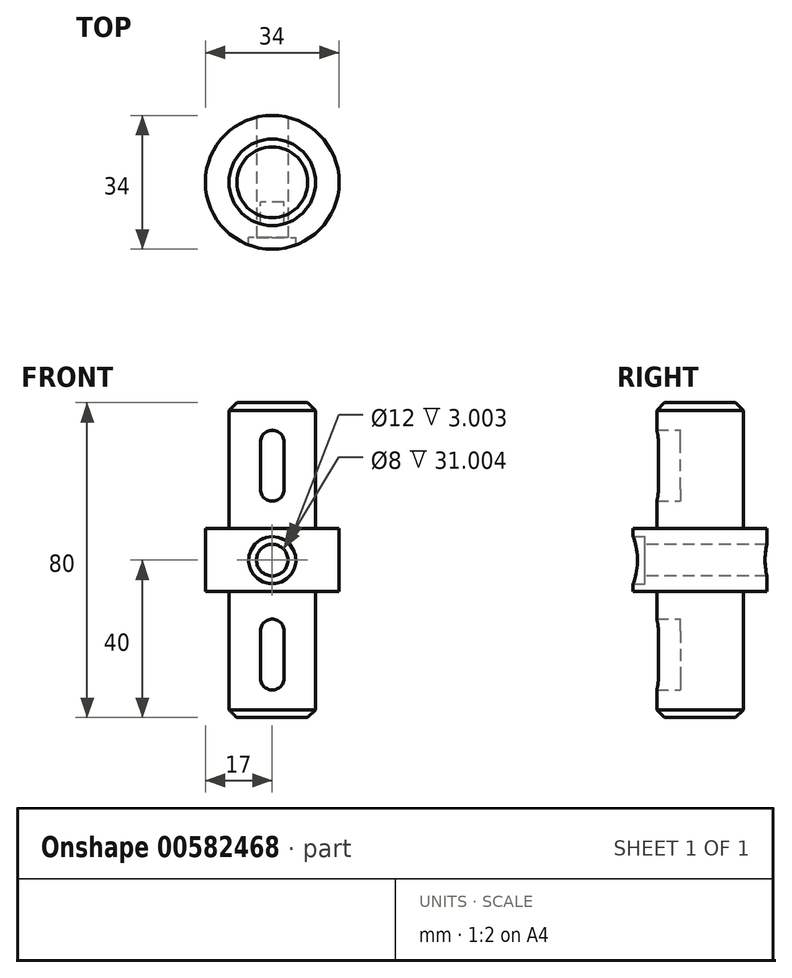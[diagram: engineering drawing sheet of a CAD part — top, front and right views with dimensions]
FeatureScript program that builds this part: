
annotation { "Feature Type Name" : "Feature", "Feature Type Description" : "" }
export const myFeature = defineFeature(function(context is Context, id is Id, definition is map)
    precondition{}
    {
        {
            var Q0;
            Q0=qCreatedBy(makeId("Top.planeOp"),FACE);
            var sketch = newSketch(context, id + "F0", { "sketchPlane" : qUnion([Q0])});
            skCircle(sketch, "E0", {"center": v(0, 0) * mm, "radius": 17 * mm});
            skSolve(sketch);
        }
        {
            var Q0;
            Q0=makeQuery(id+"F0.imprint","IMPRINT",FACE,{"disambiguationData":[TD([[makeQuery(id+"F0.imprint","IMPRINT",EDGE,{"derivedFrom":sQuery(id+"F0.wireOp",EDGE,"E0")}),1.0]])]});
            extrude(context, id + "F1", {"entities" : qUnion([Q0]), "depth" : 16 * mm, "offsetDistance" : 25 * mm});
        }
        {
            var Q0;
            Q0=makeQuery(id+"F1.opExtrude","CAP_FACE",FACE,{"disambiguationData":[OSD([sQuery(id+"F0.wireOp",EDGE,"E0")])],"isStart":false});
            var sketch = newSketch(context, id + "F2", { "sketchPlane" : qUnion([Q0])});
            skCircle(sketch, "E1", {"center": v(0, 0) * mm, "radius": 11 * mm});
            skSolve(sketch);
        }
        {
            var Q0;
            Q0=makeQuery(id+"F2.imprint","IMPRINT",FACE,{"disambiguationData":[TD([[makeQuery(id+"F2.imprint","IMPRINT",EDGE,{"derivedFrom":sQuery(id+"F2.wireOp",EDGE,"E1")}),1.0]])]});
            extrude(context, id + "F3", {"entities" : qUnion([Q0]), "operationType" : NewBodyOperationType.ADD, "depth" : 32 * mm, "offsetDistance" : 25 * mm});
        }
        {
            var Q0;
            Q0=makeQuery(id+"F3.opExtrude","CAP_FACE",FACE,{"disambiguationData":[OSD([sQuery(id+"F2.wireOp",EDGE,"E1")])],"isStart":false});
            chamfer(context, id + "F4", {"entities" : qUnion([Q0]), "width" : 2 * mm, "tangentPropagation" : true});
        }
        {
            var Q0;
            Q0=makeQuery(id+"F1.opExtrude","CAP_FACE",FACE,{"disambiguationData":[OSD([sQuery(id+"F0.wireOp",EDGE,"E0")])],"isStart":true});
            var sketch = newSketch(context, id + "F5", { "sketchPlane" : qUnion([Q0])});
            skCircle(sketch, "E2", {"center": v(0, 0) * mm, "radius": 11 * mm});
            skSolve(sketch);
        }
        {
            var Q0;
            Q0=makeQuery(id+"F5.imprint","IMPRINT",FACE,{"disambiguationData":[TD([[makeQuery(id+"F5.imprint","IMPRINT",EDGE,{"derivedFrom":sQuery(id+"F5.wireOp",EDGE,"E2")}),1.0]])]});
            extrude(context, id + "F6", {"entities" : qUnion([Q0]), "operationType" : NewBodyOperationType.ADD, "depth" : 32 * mm, "offsetDistance" : 25 * mm});
        }
        {
            var Q0;
            Q0=makeQuery(id+"F6.opExtrude","CAP_FACE",FACE,{"disambiguationData":[OSD([sQuery(id+"F5.wireOp",EDGE,"E2")])],"isStart":false});
            chamfer(context, id + "F7", {"entities" : qUnion([Q0]), "width" : 2 * mm, "tangentPropagation" : true});
        }
        {
            var Q0;
            Q0=qCreatedBy(makeId("Front.planeOp"),FACE);
            cPlane(context, id + "F8", {"entities" : qUnion([Q0]), "cplaneType" : CPlaneType.OFFSET, "offset" : 14 * mm, "width" : 150 * mm, "height" : 150 * mm});
        }
        {
            var Q0;
            Q0=qCreatedBy(id+"F8.planeOp",FACE);
            var sketch = newSketch(context, id + "F9", { "sketchPlane" : qUnion([Q0])});
            skCircle(sketch, "E3", {"center": v(0, 8) * mm, "radius": 6 * mm});
            skSolve(sketch);
        }
        {
            var Q0;
            Q0 = qSketchRegion(id + "F9", true);
            extrude(context, id + "F10", {"entities" : qUnion([Q0]), "operationType" : NewBodyOperationType.REMOVE, "endBound" : BoundingType.THROUGH_ALL, "depth" : 25 * mm, "offsetDistance" : 25 * mm});
        }
        {
            var Q0;
            Q0=makeQuery(id+"F10.boolean.opBoolean","COPY",FACE,{"derivedFrom":makeQuery(id+"F10.opExtrude","CAP_FACE",FACE,{"disambiguationData":[OSD([sQuery(id+"F9.wireOp",EDGE,"E3")])],"isStart":true})});
            var sketch = newSketch(context, id + "F11", { "sketchPlane" : qUnion([Q0])});
            skCircle(sketch, "E4", {"center": v(0, 8) * mm, "radius": 4 * mm});
            skSolve(sketch);
        }
        {
            var Q0;
            Q0 = qSketchRegion(id + "F11", true);
            extrude(context, id + "F12", {"entities" : qUnion([Q0]), "operationType" : NewBodyOperationType.REMOVE, "endBound" : BoundingType.THROUGH_ALL, "oppositeDirection" : true, "depth" : 25 * mm, "offsetDistance" : 25 * mm});
        }
        {
            var Q0;
            Q0=qCreatedBy(id+"F8.planeOp",FACE);
            cPlane(context, id + "F13", {"entities" : qUnion([Q0]), "cplaneType" : CPlaneType.OFFSET, "offset" : 9 * mm, "oppositeDirection" : true, "width" : 150 * mm, "height" : 150 * mm});
        }
        {
            var Q0;
            Q0=qCreatedBy(id+"F13.planeOp",FACE);
            var sketch = newSketch(context, id + "F14", { "sketchPlane" : qUnion([Q0])});
            skLineSegment(sketch, "E5", {"start": v(3, 26) * mm, "end": v(3, 38) * mm});
            skLineSegment(sketch, "E6", {"start": v(-3, 26) * mm, "end": v(-3, 38) * mm});
            skArc(sketch, "E7", {"start": v(3, 38) * mm, "mid": v(0, 41) * mm, "end": v(-3, 38) * mm});
            skArc(sketch, "E8", {"start": v(-3, 26) * mm, "mid": v(0, 23) * mm, "end": v(3, 26) * mm});
            skSolve(sketch);
        }
        {
            var Q0;
            Q0=makeQuery(id+"F14.imprint","IMPRINT",FACE,{"disambiguationData":[TD([[makeQuery(id+"F14.imprint","IMPRINT",EDGE,{"derivedFrom":sQuery(id+"F14.wireOp",EDGE,"E5")}),1.0]])]});
            extrude(context, id + "F15", {"entities" : qUnion([Q0]), "operationType" : NewBodyOperationType.REMOVE, "endBound" : BoundingType.THROUGH_ALL, "depth" : 25 * mm, "offsetDistance" : 25 * mm});
        }
        {
            var Q0;
            Q0=qCreatedBy(id+"F13.planeOp",FACE);
            var sketch = newSketch(context, id + "F16", { "sketchPlane" : qUnion([Q0])});
            skLineSegment(sketch, "E9", {"start": v(3, -10) * mm, "end": v(3, -22) * mm});
            skLineSegment(sketch, "E10", {"start": v(-3, -10) * mm, "end": v(-3, -22) * mm});
            skArc(sketch, "E11", {"start": v(3, -10) * mm, "mid": v(0, -7) * mm, "end": v(-3, -10) * mm});
            skArc(sketch, "E12", {"start": v(-3, -22) * mm, "mid": v(0, -25) * mm, "end": v(3, -22) * mm});
            skSolve(sketch);
        }
        {
            var Q0;
            Q0 = qSketchRegion(id + "F16", true);
            extrude(context, id + "F17", {"entities" : qUnion([Q0]), "operationType" : NewBodyOperationType.REMOVE, "endBound" : BoundingType.THROUGH_ALL, "depth" : 25 * mm, "offsetDistance" : 25 * mm});
        }
    });
